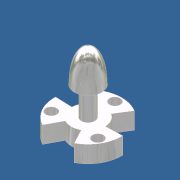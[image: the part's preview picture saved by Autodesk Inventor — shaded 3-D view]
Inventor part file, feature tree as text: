
AUTODESK INVENTOR PART (.ipt)
format: ipt  version: unknown  size: 301,056 bytes
history: native  units: mm
features: sketch x9, extrude x8, reference x5, pattern_circular x1, thread x1, chamfer x1, revolve x1
ambient origin geometry x8: Origin, YZ Plane, XZ Plane, XY Plane, X Axis, Y Axis, Z Axis, Center Point
bodies: Solid1 (feature_tree)
feature tree (26):
  extrude  "Extrusion1"  Depth=20.0mm
  extrude  "Extrusion2"  Depth=5.0mm TaperAngle=0.0deg
  pattern_circular  "Circular Pattern1"  Count=3 Angle=360.0deg
  extrude  "Extrusion3"  Depth=5.0mm TaperAngle=0.0deg
  extrude  "Extrusion4"  Depth=3.2mm
  extrude  "Extrusion5"  Depth=3.0mm TaperAngle=0.0deg
  extrude  "Extrusion6"  Depth=8.0mm TaperAngle=0.0deg
  extrude  "Extrusion7"  Depth=0.4mm TaperAngle=0.0deg
  thread  "Thread1"  [1 undecoded]
  chamfer  "Chamfer1"  Distance=10.0mm
  revolve  "Revolution1"  Angle=45.0deg
  extrude  "Extrusion8"  Depth=8.0mm
  sketch  "Sketch1"  dims[d0=8.0mm d1=20.0mm]
  reference  "Reference1"
  reference  "Reference2"
  reference  "Reference3"
  sketch  "Sketch2"  dims[d2=5.0mm d3=0.0mm d4=5.0mm d5=0.0mm d6=30.0mm d7=360.0deg]
  reference  "Reference4"
  reference  "Reference5"
  sketch  "Sketch3"  dims[d9=10.0mm d10=5.0mm d11=0.0mm]
  sketch  "Sketch4"  dims[d12=3.2mm d13=3.2mm]
  sketch  "Sketch5"  dims[d14=3.2mm d15=3.0mm d16=0.0mm]
  sketch  "Sketch6"  dims[d17=4.0mm d18=8.0mm d19=0.0mm]
  sketch  "Sketch7"  dims[d20=3.8mm d21=0.4mm d22=0.0mm d23=4.0mm d24=10.0mm d25=0.0mm]
  sketch  "Sketch8"  dims[d26=10.0mm d27=0.0mm d28=0.4mm d29=2.0mm d30=45.0deg]
  sketch  "Sketch9"  dims[d31=90.0deg d32=8.0mm d33=9.924142mm d34=1.5mm d35=20.0mm d36=0.0mm]
note: 1 required parameter value undecoded (feature->parameter linkage not recoverable at this tier; creation-order binding heuristic only, values carry confidence <= 0.55)
